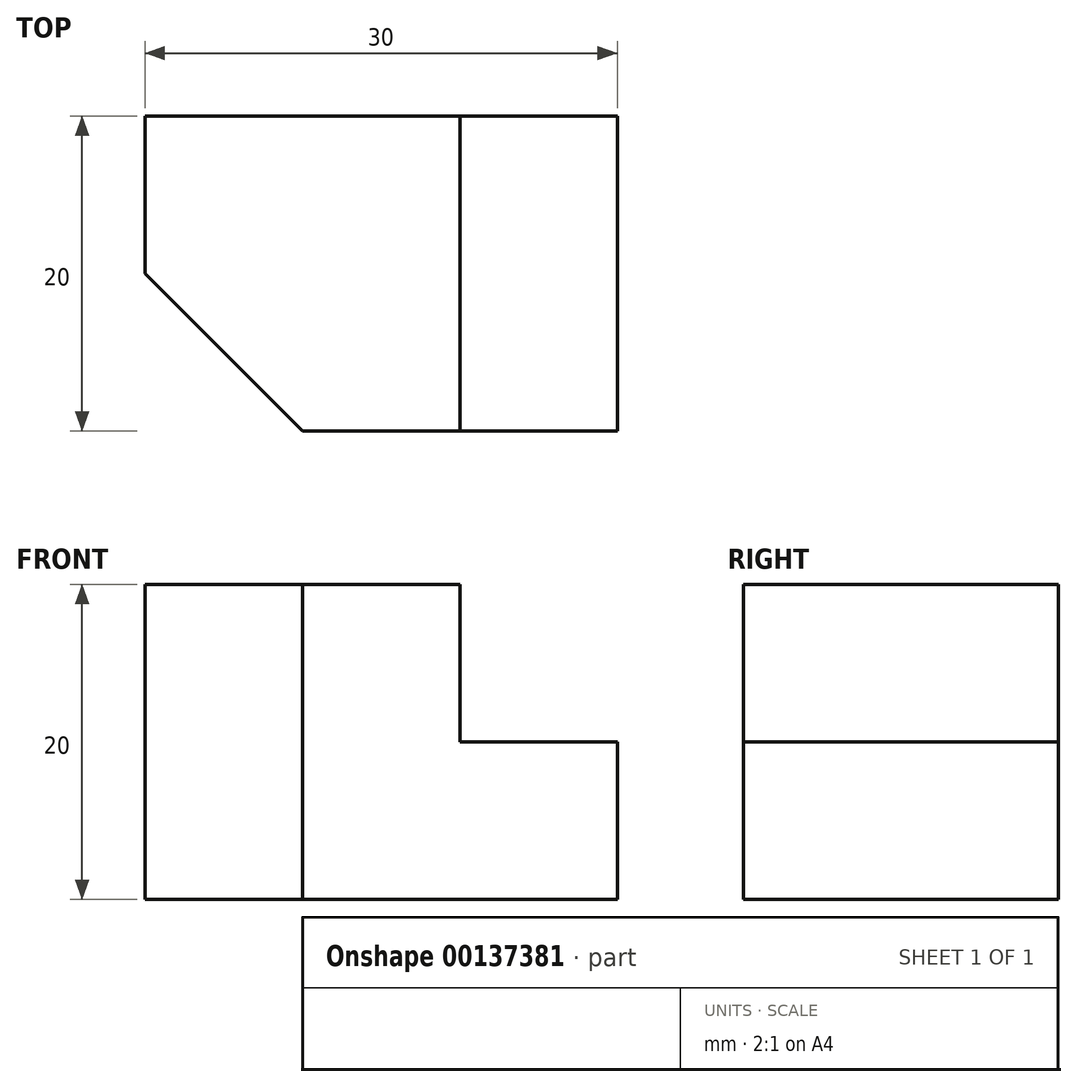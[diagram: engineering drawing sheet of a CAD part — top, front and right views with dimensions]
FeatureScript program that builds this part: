
annotation { "Feature Type Name" : "Feature", "Feature Type Description" : "" }
export const myFeature = defineFeature(function(context is Context, id is Id, definition is map)
    precondition{}
    {
        {
            var Q0;
            Q0=qCreatedBy(makeId("Front.planeOp"),FACE);
            var sketch = newSketch(context, id + "F0", { "sketchPlane" : qUnion([Q0])});
            skLineSegment(sketch, "E0", {"start": v(0, 0) * mm, "end": v(30, 0) * mm});
            skLineSegment(sketch, "E1", {"start": v(30, 0) * mm, "end": v(30, 10) * mm});
            skLineSegment(sketch, "E2", {"start": v(30, 10) * mm, "end": v(20, 10) * mm});
            skLineSegment(sketch, "E3", {"start": v(20, 10) * mm, "end": v(20, 20) * mm});
            skLineSegment(sketch, "E4", {"start": v(20, 20) * mm, "end": v(10, 20) * mm});
            skLineSegment(sketch, "E5", {"start": v(10, 20) * mm, "end": v(0, 20) * mm});
            skLineSegment(sketch, "E6", {"start": v(0, 20) * mm, "end": v(0, 0) * mm});
            skLineSegment(sketch, "E7", {"start": v(10, 20) * mm, "end": v(10, 0) * mm});
            skSolve(sketch);
        }
        {
            var Q0;
            Q0=qSketchRegion(id+"F0",true);
            extrude(context, id + "F1", {"entities" : qUnion([Q0]), "endBound" : BoundingType.SYMMETRIC, "oppositeDirection" : true, "depth" : 20 * mm});
        }
        {
            var Q0;
            Q0=makeQuery(id+"F1.opExtrude","SWEPT_FACE",FACE,{"disambiguationData":[OSD([sQuery(id+"F0.wireOp",EDGE,"E4"),sQuery(id+"F0.wireOp",EDGE,"E5")])]});
            var sketch = newSketch(context, id + "F2", { "sketchPlane" : qUnion([Q0])});
            skLineSegment(sketch, "E8", {"start": v(10, -10) * mm, "end": v(0, 0) * mm});
            skSolve(sketch);
        }
        {
            var Q0;
            Q0=qSketchRegion(id+"F2",true);
            var Q1;
            {var subQ0=sQuery(id+"F2.wireOp",EDGE,"E8");Q1=makeQuery(id+"F2.imprint","IMPRINT",FACE,{"disambiguationData":[TD([[makeQuery(id+"F2.imprint","IMPRINT",EDGE,{"derivedFrom":subQ0}),1.0]])]});}
            extrude(context, id + "F3", {"entities" : qUnion([Q0, Q1]), "operationType" : NewBodyOperationType.REMOVE, "endBound" : BoundingType.THROUGH_ALL, "oppositeDirection" : true, "depth" : 25 * mm});
        }
    });
